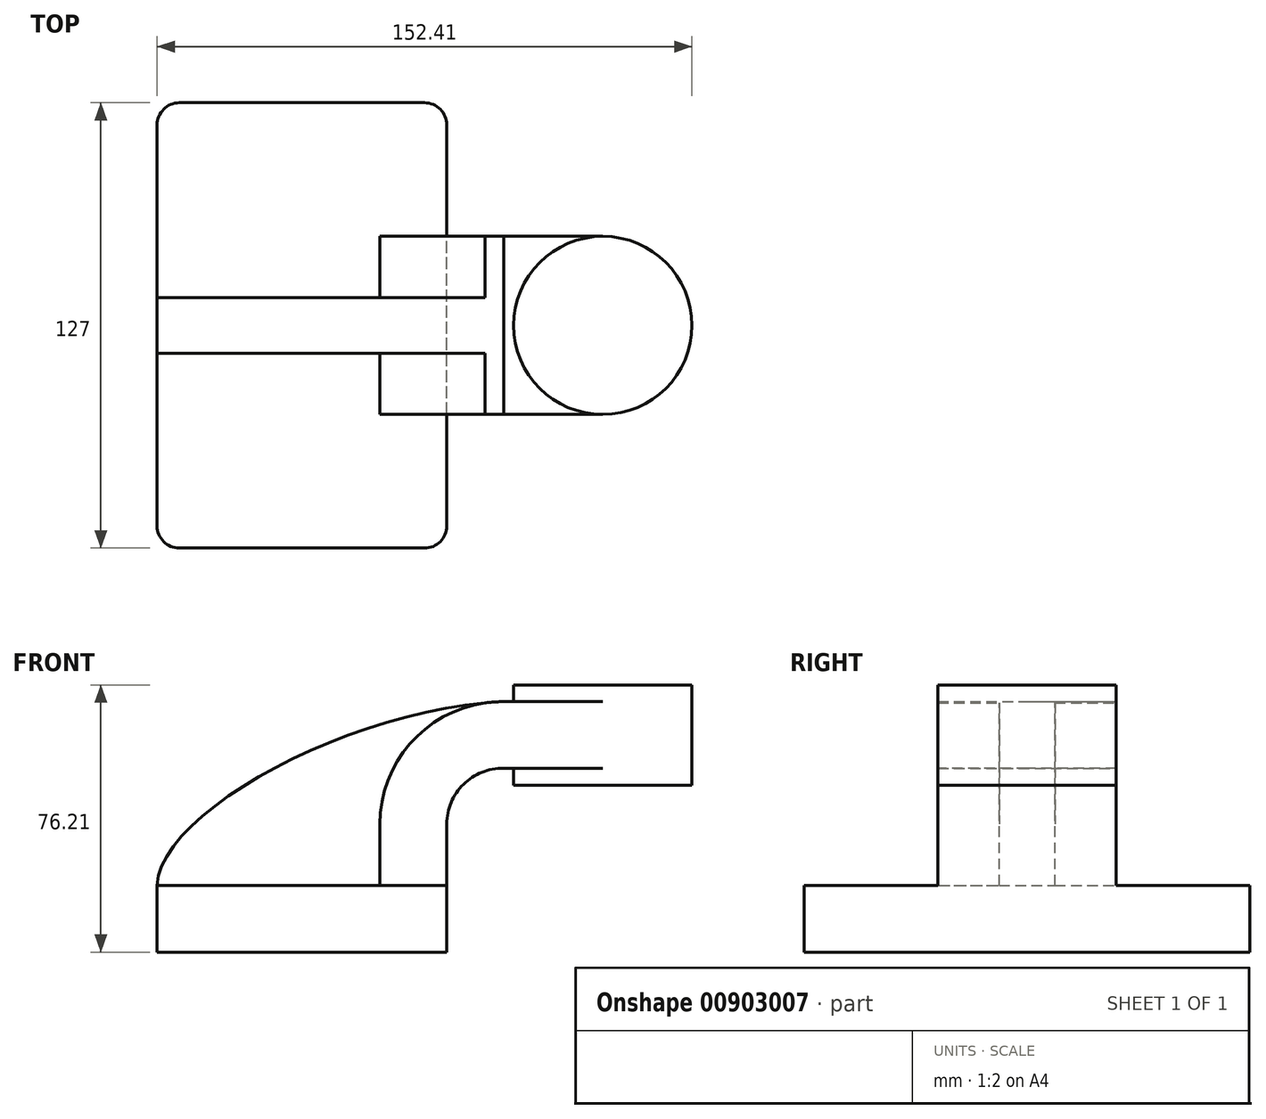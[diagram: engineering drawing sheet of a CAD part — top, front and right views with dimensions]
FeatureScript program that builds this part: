
annotation { "Feature Type Name" : "Feature", "Feature Type Description" : "" }
export const myFeature = defineFeature(function(context is Context, id is Id, definition is map)
    precondition{}
    {
        {
            var Q0;
            Q0=qCreatedBy(makeId("Front.planeOp"),FACE);
            var sketch = newSketch(context, id + "F0", { "sketchPlane" : qUnion([Q0])});
            skLineSegment(sketch, "E0.bottom", {"start": v(41.28, -9.52) * mm, "end": v(-41.28, -9.53) * mm});
            skLineSegment(sketch, "E0.top", {"start": v(41.28, 9.53) * mm, "end": v(-41.28, 9.53) * mm});
            skLineSegment(sketch, "E0.left", {"start": v(41.28, -9.52) * mm, "end": v(41.28, 9.53) * mm});
            skLineSegment(sketch, "E0.right", {"start": v(-41.28, -9.53) * mm, "end": v(-41.28, 9.53) * mm});
            skPoint(sketch, "E0.middle", {"position": v(0, 0) * mm});
            skLineSegment(sketch, "E1.bottom", {"start": v(111.12, 66.68) * mm, "end": v(60.32, 66.68) * mm});
            skLineSegment(sketch, "E1.top", {"start": v(111.12, 38.1) * mm, "end": v(60.32, 38.1) * mm});
            skLineSegment(sketch, "E1.left", {"start": v(111.12, 66.68) * mm, "end": v(111.12, 38.1) * mm});
            skLineSegment(sketch, "E1.right", {"start": v(60.32, 66.68) * mm, "end": v(60.32, 38.1) * mm});
            skPoint(sketch, "E1.middle", {"position": v(85.72, 52.39) * mm});
            skLineSegment(sketch, "E2", {"start": v(41.28, 9.53) * mm, "end": v(41.28, 27) * mm});
            skArc(sketch, "E3", {"start": v(41.27, 27) * mm, "mid": v(46.01, 38.32) * mm, "end": v(57.4, 42.88) * mm});
            skLineSegment(sketch, "E4", {"start": v(57.4, 42.88) * mm, "end": v(85.72, 42.88) * mm});
            skArc(sketch, "E5.1", {"start": v(22.23, 27) * mm, "mid": v(32.59, 51.83) * mm, "end": v(57.52, 61.93) * mm});
            skLineSegment(sketch, "E5.2", {"start": v(22.22, 9.53) * mm, "end": v(22.22, 27) * mm});
            skLineSegment(sketch, "E6", {"start": v(85.72, 38.1) * mm, "end": v(85.72, 66.68) * mm});
            skFitSpline(sketch, "E7", {"points": [v(-41.28, 9.52) * mm, v(57.52, 61.93) * mm], "startDerivative": vector(2.48, 63.56) * mm, "endDerivative": vector(129.1, 5.4) * mm});
            skLineSegment(sketch, "E8", {"start": v(85.72, 61.93) * mm, "end": v(57.52, 61.93) * mm});
            skSolve(sketch);
        }
        {
            var Q0;
            Q0=makeQuery(id+"F0.imprint","IMPRINT",FACE,{"disambiguationData":[TD([[makeQuery(id+"F0.imprint","IMPRINT",EDGE,{"derivedFrom":sQuery(id+"F0.wireOp",EDGE,"E0.bottom")}),-1.0]])]});
            extrude(context, id + "F1", {"entities" : qUnion([Q0]), "depth" : 127 * mm, "offsetDistance" : 25.4 * mm, "symmetric" : true});
        }
        {
            var Q0;
            {var subQ1=sQuery(id+"F0.wireOp",EDGE,"E2");Q0=makeQuery(id+"F0.imprint","IMPRINT",FACE,{"disambiguationData":[TD([[makeQuery(id+"F0.imprint","IMPRINT",EDGE,{"derivedFrom":subQ1}),1.0]])]});}
            var Q1;
            {var subQ0=sQuery(id+"F0.wireOp",EDGE,"E8");var subQ1=sQuery(id+"F0.wireOp",EDGE,"E1.right");var subQ2=makeQuery(id+"F0.imprint","INTERSECT",VERTEX,{"derivedFrom":[subQ1,subQ0]});Q1=makeQuery(id+"F0.imprint","IMPRINT",FACE,{"disambiguationData":[TD([[makeQuery(id+"F0.imprint","IMPRINT",EDGE,{"disambiguationData":[TD([[subQ2,-1.0]])],"derivedFrom":subQ1}),1.0]])]});}
            extrude(context, id + "F2", {"entities" : qUnion([Q0, Q1]), "operationType" : NewBodyOperationType.ADD, "depth" : 50.8 * mm, "offsetDistance" : 25.4 * mm, "symmetric" : true});
        }
        {
            var Q0;
            {var subQ3=sQuery(id+"F0.wireOp",EDGE,"E5.2");Q0=makeQuery(id+"F0.imprint","IMPRINT",FACE,{"disambiguationData":[TD([[makeQuery(id+"F0.imprint","IMPRINT",EDGE,{"derivedFrom":subQ3}),1.0]])]});}
            extrude(context, id + "F3", {"entities" : qUnion([Q0]), "operationType" : NewBodyOperationType.ADD, "depth" : 15.88 * mm, "offsetDistance" : 25.4 * mm, "symmetric" : true});
        }
        {
            var Q0;
            {var subQ0=sQuery(id+"F0.wireOp",EDGE,"E1.left");Q0=makeQuery(id+"F0.imprint","IMPRINT",FACE,{"disambiguationData":[TD([[makeQuery(id+"F0.imprint","IMPRINT",EDGE,{"derivedFrom":subQ0}),-1.0]])]});}
            var Q1;
            Q1=sQuery(id+"F0.wireOp",EDGE,"E6");
            revolve(context, id + "F4", {"operationType" : NewBodyOperationType.ADD, "surfaceOperationType" : NewSurfaceOperationType.NEW, "entities" : qUnion([Q0]), "axis" : qUnion([Q1]), "revolveType" : RevolveType.FULL});
        }
        {
            var Q0;
            Q0=makeQuery(id+"F1.opExtrude","CAP_EDGE",EDGE,{"disambiguationData":[OSD([sQuery(id+"F0.wireOp",EDGE,"E0.left")])],"isStart":false});
            var Q1;
            Q1=makeQuery(id+"F1.opExtrude","CAP_EDGE",EDGE,{"disambiguationData":[OSD([sQuery(id+"F0.wireOp",EDGE,"E0.right")])],"isStart":false});
            var Q2;
            Q2=makeQuery(id+"F1.opExtrude","CAP_EDGE",EDGE,{"disambiguationData":[OSD([sQuery(id+"F0.wireOp",EDGE,"E0.right")])],"isStart":true});
            var Q3;
            Q3=makeQuery(id+"F1.opExtrude","CAP_EDGE",EDGE,{"disambiguationData":[OSD([sQuery(id+"F0.wireOp",EDGE,"E0.left")])],"isStart":true});
            fillet(context, id + "F5", {"entities" : qUnion([Q0, Q1, Q2, Q3]), "radius" : 6.35 * mm, "tangentPropagation" : true, "allowEdgeOverflow" : false});
        }
    });
